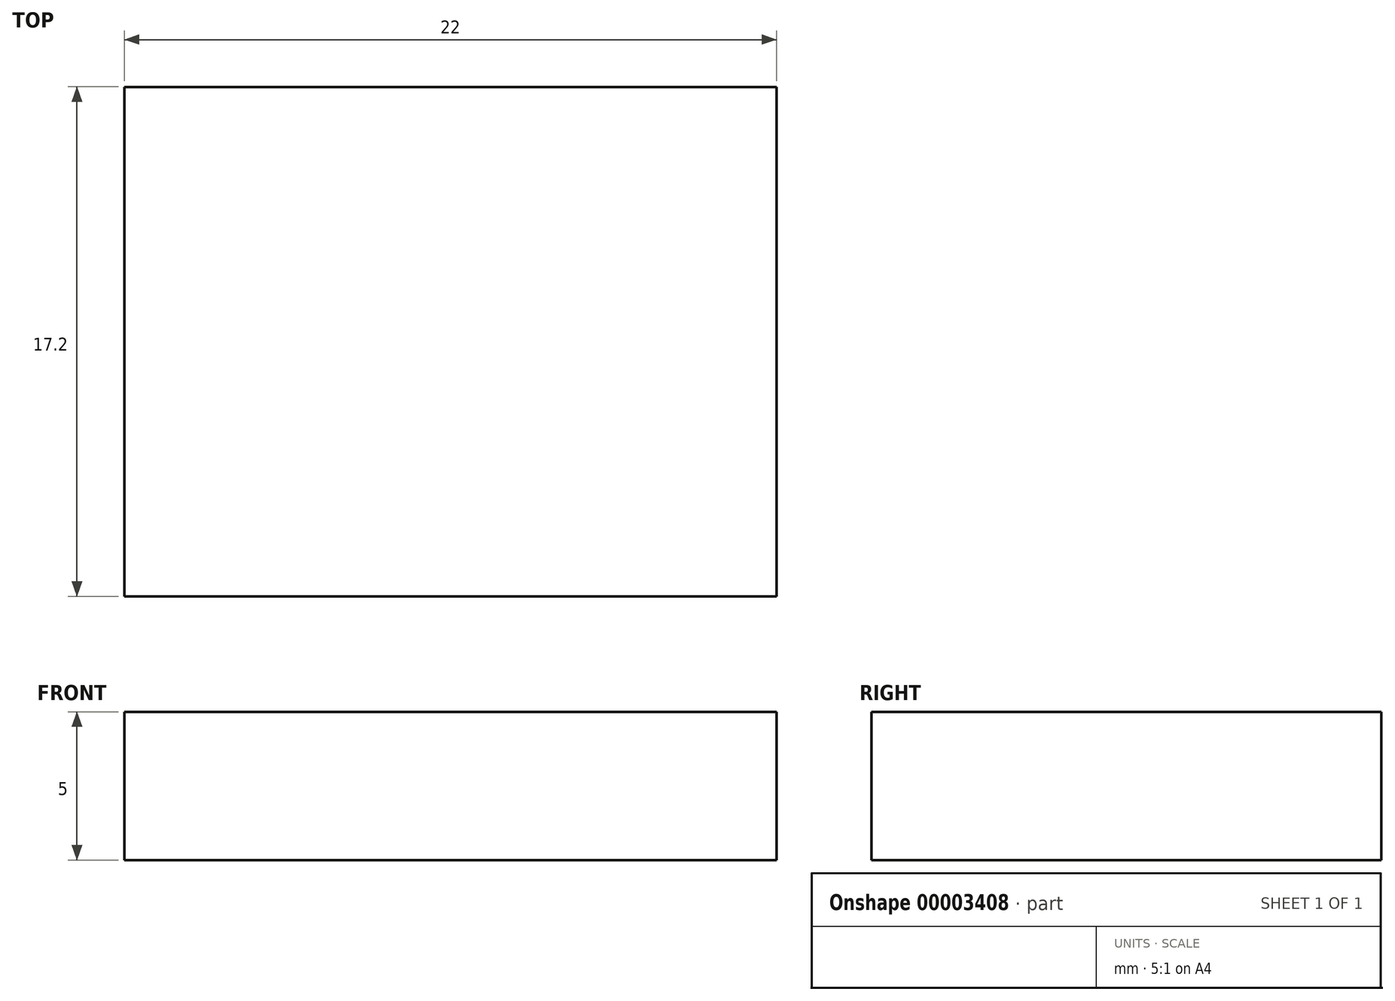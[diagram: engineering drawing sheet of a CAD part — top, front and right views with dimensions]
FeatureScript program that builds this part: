
annotation { "Feature Type Name" : "Feature", "Feature Type Description" : "" }
export const myFeature = defineFeature(function(context is Context, id is Id, definition is map)
    precondition{}
    {
        {
            var Q0;
            Q0=qCreatedBy(makeId("Top.planeOp"),FACE);
            var sketch = newSketch(context, id + "F0", { "sketchPlane" : qUnion([Q0])});
            skLineSegment(sketch, "E0.bottom", {"start": v(-55.16, -17.92) * mm, "end": v(-33.16, -17.92) * mm});
            skLineSegment(sketch, "E0.top", {"start": v(-55.16, -35.12) * mm, "end": v(-33.16, -35.12) * mm});
            skLineSegment(sketch, "E0.left", {"start": v(-55.16, -17.92) * mm, "end": v(-55.16, -35.12) * mm});
            skLineSegment(sketch, "E0.right", {"start": v(-33.16, -17.92) * mm, "end": v(-33.16, -35.12) * mm});
            skSolve(sketch);
        }
        {
            var Q0;
            Q0=makeQuery(id+"F0.imprint","IMPRINT",FACE,{"disambiguationData":[TD([[makeQuery(id+"F0.imprint","IMPRINT",EDGE,{"derivedFrom":sQuery(id+"F0.wireOp",EDGE,"E0.bottom")}),-1.0]])]});
            extrude(context, id + "F1", {"entities" : qUnion([Q0]), "depth" : 5 * mm});
        }
    });
